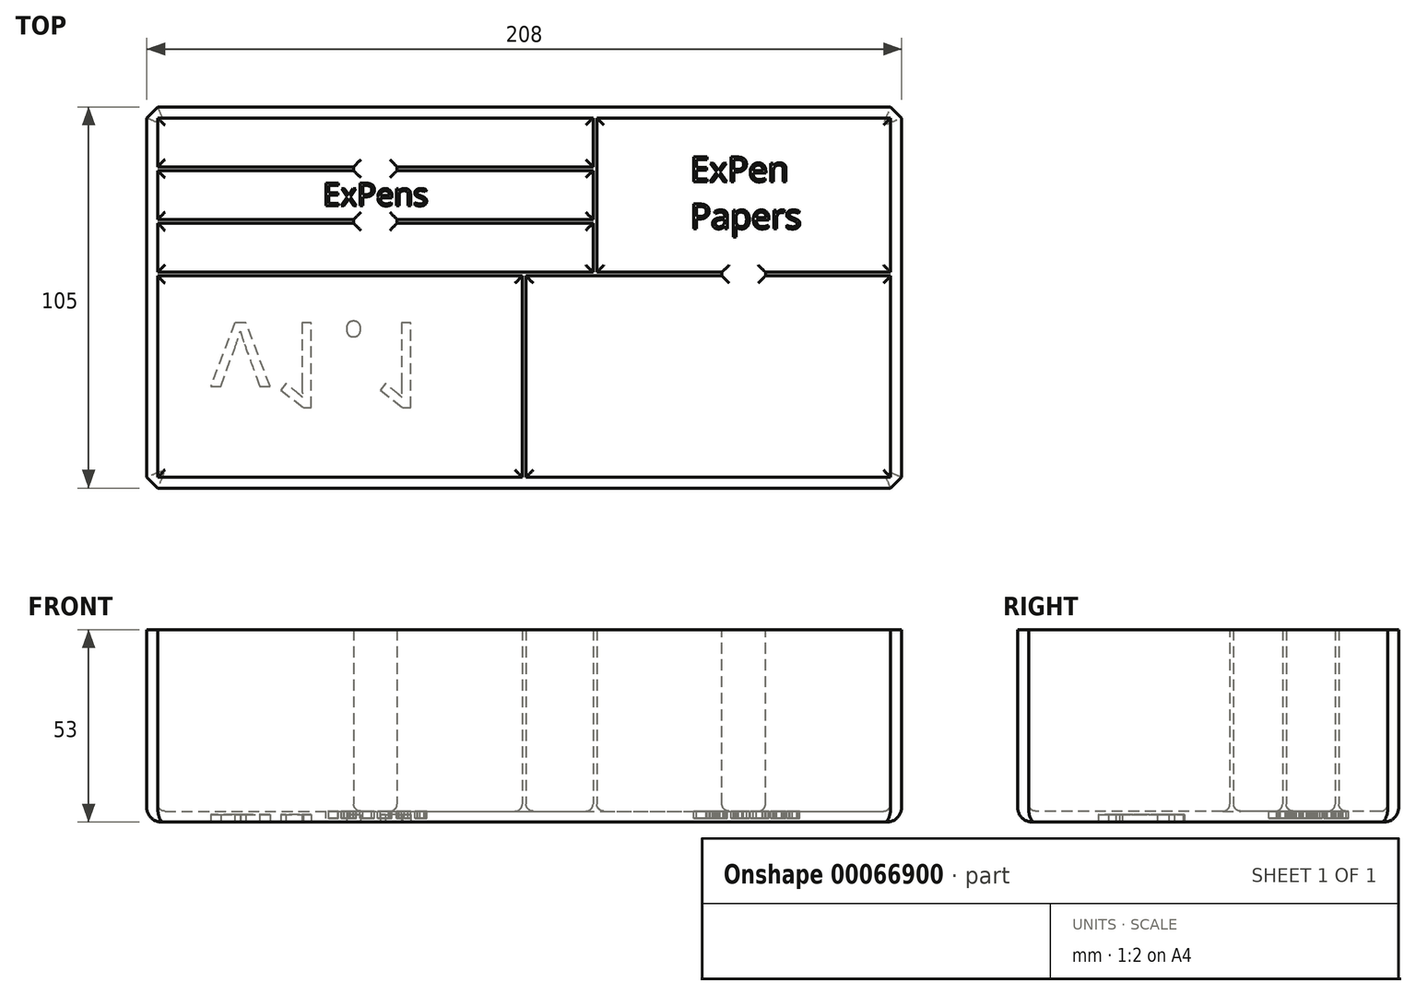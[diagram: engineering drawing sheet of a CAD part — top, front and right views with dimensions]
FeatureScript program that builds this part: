
annotation { "Feature Type Name" : "Feature", "Feature Type Description" : "" }
export const myFeature = defineFeature(function(context is Context, id is Id, definition is map)
    precondition{}
    {
        {
            var Q0;
            Q0=qCreatedBy(makeId("Top.planeOp"),FACE);
            var sketch = newSketch(context, id + "F0", { "sketchPlane" : qUnion([Q0])});
            skLineSegment(sketch, "E0.bottom", {"start": v(-42.14, 90.11) * mm, "end": v(165.86, 90.11) * mm});
            skLineSegment(sketch, "E0.top", {"start": v(-42.14, -14.89) * mm, "end": v(165.86, -14.89) * mm});
            skLineSegment(sketch, "E0.left", {"start": v(-42.14, 90.11) * mm, "end": v(-42.14, -14.89) * mm});
            skLineSegment(sketch, "E0.right", {"start": v(165.86, 90.11) * mm, "end": v(165.86, -14.89) * mm});
            skSolve(sketch);
        }
        {
            var Q0;
            Q0 = qSketchRegion(id + "F0", true);
            extrude(context, id + "F1", {"entities" : qUnion([Q0]), "depth" : 53 * mm});
        }
        {
            var Q0;
            Q0=makeQuery(id+"F1.opExtrude","CAP_FACE",FACE,{"disambiguationData":[OSD([sQuery(id+"F0.wireOp",EDGE,"E0.bottom"),sQuery(id+"F0.wireOp",EDGE,"E0.top"),sQuery(id+"F0.wireOp",EDGE,"E0.left"),sQuery(id+"F0.wireOp",EDGE,"E0.right")])],"isStart":false});
            shell(context, id + "F2", {"entities" : qUnion([Q0]), "thickness" : 3 * mm});
        }
        {
            var Q0;
            Q0=makeQuery(id+"F2.opShell","OFFSET_FACE",FACE,{"disambiguationData":[OSD([sQuery(id+"F0.wireOp",EDGE,"E0.bottom"),sQuery(id+"F0.wireOp",EDGE,"E0.top"),sQuery(id+"F0.wireOp",EDGE,"E0.left"),sQuery(id+"F0.wireOp",EDGE,"E0.right")])]});
            var sketch = newSketch(context, id + "F3", { "sketchPlane" : qUnion([Q0])});
            skLineSegment(sketch, "E1.bottom", {"start": v(-39.14, 73.61) * mm, "end": v(81.86, 73.61) * mm});
            skLineSegment(sketch, "E1.top", {"start": v(-39.14, 72.61) * mm, "end": v(81.86, 72.61) * mm});
            skLineSegment(sketch, "E1.left", {"start": v(-39.14, 73.61) * mm, "end": v(-39.14, 72.61) * mm});
            skLineSegment(sketch, "E1.right", {"start": v(162.86, 73.61) * mm, "end": v(162.86, 72.61) * mm});
            skLineSegment(sketch, "E2.bottom", {"start": v(-39.14, 59.11) * mm, "end": v(81.86, 59.11) * mm});
            skLineSegment(sketch, "E2.top", {"start": v(-39.14, 58.11) * mm, "end": v(81.86, 58.11) * mm});
            skLineSegment(sketch, "E2.left", {"start": v(-39.14, 59.11) * mm, "end": v(-39.14, 58.11) * mm});
            skLineSegment(sketch, "E2.right", {"start": v(162.86, 59.11) * mm, "end": v(162.86, 58.11) * mm});
            skLineSegment(sketch, "E3.bottom", {"start": v(-39.14, 44.61) * mm, "end": v(162.86, 44.61) * mm});
            skLineSegment(sketch, "E3.top", {"start": v(-39.14, 43.61) * mm, "end": v(162.86, 43.61) * mm});
            skLineSegment(sketch, "E3.left", {"start": v(-39.14, 44.61) * mm, "end": v(-39.14, 43.61) * mm});
            skLineSegment(sketch, "E3.right", {"start": v(162.86, 44.61) * mm, "end": v(162.86, 43.61) * mm});
            skLineSegment(sketch, "E4.bottom", {"start": v(62.36, 43.61) * mm, "end": v(61.36, 43.61) * mm});
            skLineSegment(sketch, "E4.top", {"start": v(62.36, -11.89) * mm, "end": v(61.36, -11.89) * mm});
            skLineSegment(sketch, "E4.left", {"start": v(62.36, 43.61) * mm, "end": v(62.36, -11.89) * mm});
            skLineSegment(sketch, "E4.right", {"start": v(61.36, 43.61) * mm, "end": v(61.36, -11.89) * mm});
            skLineSegment(sketch, "E5.bottom", {"start": v(80.86, 87.11) * mm, "end": v(81.86, 87.11) * mm});
            skLineSegment(sketch, "E5.top", {"start": v(80.86, 44.61) * mm, "end": v(81.86, 44.61) * mm});
            skLineSegment(sketch, "E5.left", {"start": v(80.86, 87.11) * mm, "end": v(80.86, 44.61) * mm});
            skLineSegment(sketch, "E5.right", {"start": v(81.86, 87.11) * mm, "end": v(81.86, 44.61) * mm});
            skSolve(sketch);
        }
        {
            var Q0;
            Q0 = qSketchRegion(id + "F3", true);
            extrude(context, id + "F4", {"entities" : qUnion([Q0]), "operationType" : NewBodyOperationType.ADD, "depth" : 50 * mm});
        }
        {
            var Q0;
            Q0=makeQuery(id+"F1.opExtrude","SWEPT_EDGE",EDGE,{"disambiguationData":[OSD([sQuery(id+"F0.wireOp",EDGE,"E0.top"),sQuery(id+"F0.wireOp",EDGE,"E0.right")])]});
            var Q1;
            Q1=makeQuery(id+"F1.opExtrude","SWEPT_EDGE",EDGE,{"disambiguationData":[OSD([sQuery(id+"F0.wireOp",EDGE,"E0.bottom"),sQuery(id+"F0.wireOp",EDGE,"E0.right")])]});
            var Q2;
            Q2=makeQuery(id+"F1.opExtrude","SWEPT_EDGE",EDGE,{"disambiguationData":[OSD([sQuery(id+"F0.wireOp",EDGE,"E0.top"),sQuery(id+"F0.wireOp",EDGE,"E0.left")])]});
            var Q3;
            Q3=makeQuery(id+"F1.opExtrude","SWEPT_EDGE",EDGE,{"disambiguationData":[OSD([sQuery(id+"F0.wireOp",EDGE,"E0.bottom"),sQuery(id+"F0.wireOp",EDGE,"E0.left")])]});
            chamfer(context, id + "F5", {"entities" : qUnion([Q0, Q1, Q2, Q3]), "width" : 3 * mm, "tangentPropagation" : true});
        }
        {
            var Q0;
            Q0=makeQuery(id+"F1.opExtrude","CAP_FACE",FACE,{"disambiguationData":[OSD([sQuery(id+"F0.wireOp",EDGE,"E0.bottom"),sQuery(id+"F0.wireOp",EDGE,"E0.top"),sQuery(id+"F0.wireOp",EDGE,"E0.left"),sQuery(id+"F0.wireOp",EDGE,"E0.right")])],"isStart":true});
            fillet(context, id + "F6", {"entities" : qUnion([Q0]), "radius" : 4 * mm, "tangentPropagation" : true, "allowEdgeOverflow" : false});
        }
        {
            var Q0;
            Q0=makeQuery(id+"F4.opExtrude","SWEPT_FACE",FACE,{"disambiguationData":[OSD([sQuery(id+"F3.wireOp",EDGE,"E1.top")])]});
            var sketch = newSketch(context, id + "F7", { "sketchPlane" : qUnion([Q0])});
            skPoint(sketch, "E6", {"position": v(20.86, 3) * mm});
            skLineSegment(sketch, "E7.bottom", {"start": v(26.86, 3) * mm, "end": v(14.86, 3) * mm});
            skLineSegment(sketch, "E7.top", {"start": v(26.86, 53) * mm, "end": v(14.86, 53) * mm});
            skLineSegment(sketch, "E7.left", {"start": v(26.86, 3) * mm, "end": v(26.86, 53) * mm});
            skLineSegment(sketch, "E7.right", {"start": v(14.86, 3) * mm, "end": v(14.86, 53) * mm});
            skSolve(sketch);
        }
        {
            var Q0;
            Q0=makeQuery(id+"F7.imprint","IMPRINT",FACE,{"disambiguationData":[TD([[makeQuery(id+"F7.imprint","IMPRINT",EDGE,{"derivedFrom":sQuery(id+"F7.wireOp",EDGE,"E7.bottom")}),1.0]])]});
            extrude(context, id + "F8", {"entities" : qUnion([Q0]), "operationType" : NewBodyOperationType.REMOVE, "oppositeDirection" : true, "depth" : 10 * mm, "hasSecondDirection" : true, "secondDirectionOppositeDirection" : false, "secondDirectionDepth" : 15 * mm});
        }
        {
            var Q0;
            {var subQ0=sQuery(id+"F3.wireOp",EDGE,"E3.bottom");Q0=makeQuery(id+"F4.opExtrude","SWEPT_FACE",FACE,{"disambiguationData":[OSD([subQ0]),TDD([makeQuery(id+"F3.imprint","IMPRINT",EDGE,{"disambiguationData":[TD([[makeQuery(id+"F3.imprint","INTERSECT",VERTEX,{"derivedFrom":[subQ0,sQuery(id+"F3.wireOp",EDGE,"E5.top"),sQuery(id+"F3.wireOp",EDGE,"E5.right")]}),-1.0]])],"derivedFrom":subQ0})])]});}
            var sketch = newSketch(context, id + "F9", { "sketchPlane" : qUnion([Q0])});
            skPoint(sketch, "E8", {"position": v(-122.36, 53) * mm});
            skLineSegment(sketch, "E9.bottom", {"start": v(-128.36, 3) * mm, "end": v(-116.36, 3) * mm});
            skLineSegment(sketch, "E9.top", {"start": v(-128.36, 53) * mm, "end": v(-116.36, 53) * mm});
            skLineSegment(sketch, "E9.left", {"start": v(-128.36, 3) * mm, "end": v(-128.36, 53) * mm});
            skLineSegment(sketch, "E9.right", {"start": v(-116.36, 3) * mm, "end": v(-116.36, 53) * mm});
            skSolve(sketch);
        }
        {
            var Q0;
            Q0 = qSketchRegion(id + "F9", true);
            extrude(context, id + "F10", {"entities" : qUnion([Q0]), "operationType" : NewBodyOperationType.REMOVE, "oppositeDirection" : true, "depth" : 5 * mm});
        }
        {
            var Q0;
            {var subQ0=sQuery(id+"F0.wireOp",EDGE,"E0.top");var subQ1=sQuery(id+"F0.wireOp",EDGE,"E0.left");var subQ2=sQuery(id+"F3.wireOp",EDGE,"E4.right");Q0=makeQuery(id+"F4.boolean.opBoolean","SPLIT",FACE,{"disambiguationData":[TD([makeQuery(id+"F4.opExtrude","SWEPT_FACE",FACE,{"disambiguationData":[OSD([subQ2])]})])],"derivedFrom":makeQuery(id+"F2.opShell","OFFSET_FACE",FACE,{"disambiguationData":[OSD([sQuery(id+"F0.wireOp",EDGE,"E0.bottom"),subQ0,subQ1,sQuery(id+"F0.wireOp",EDGE,"E0.right")])]})});}
            var Q1;
            {var subQ0=sQuery(id+"F0.wireOp",EDGE,"E0.top");var subQ1=sQuery(id+"F0.wireOp",EDGE,"E0.right");var subQ6=sQuery(id+"F3.wireOp",EDGE,"E4.left");var subQ7=sQuery(id+"F0.wireOp",EDGE,"E0.bottom");var subQ8=makeQuery(id+"F2.opShell","OFFSET_FACE",FACE,{"disambiguationData":[OSD([subQ7,subQ0,sQuery(id+"F0.wireOp",EDGE,"E0.left"),subQ1])]});var subQ10=sQuery(id+"F3.wireOp",EDGE,"E5.right");Q1=makeQuery(id+"F10.boolean.opBoolean","MERGE",FACE,{"derivedFrom":[makeQuery(id+"F4.boolean.opBoolean","SPLIT",FACE,{"disambiguationData":[TD([makeQuery(id+"F4.opExtrude","SWEPT_FACE",FACE,{"disambiguationData":[OSD([subQ10])]})])],"derivedFrom":subQ8}),makeQuery(id+"F4.boolean.opBoolean","SPLIT",FACE,{"disambiguationData":[TD([makeQuery(id+"F4.opExtrude","SWEPT_FACE",FACE,{"disambiguationData":[OSD([subQ6])]})])],"derivedFrom":subQ8}),makeQuery(id+"F10.opExtrude","SWEPT_FACE",FACE,{"disambiguationData":[OSD([sQuery(id+"F9.wireOp",EDGE,"E9.bottom")])]})]});}
            var Q2;
            {var subQ0=sQuery(id+"F0.wireOp",EDGE,"E0.bottom");var subQ1=sQuery(id+"F0.wireOp",EDGE,"E0.left");var subQ4=sQuery(id+"F3.wireOp",EDGE,"E1.bottom");var subQ5=makeQuery(id+"F2.opShell","OFFSET_FACE",FACE,{"disambiguationData":[OSD([subQ0,sQuery(id+"F0.wireOp",EDGE,"E0.top"),subQ1,sQuery(id+"F0.wireOp",EDGE,"E0.right")])]});var subQ8=sQuery(id+"F3.wireOp",EDGE,"E2.top");var subQ9=sQuery(id+"F3.wireOp",EDGE,"E1.top");Q2=makeQuery(id+"F8.boolean.opBoolean","MERGE",FACE,{"derivedFrom":[makeQuery(id+"F4.boolean.opBoolean","SPLIT",FACE,{"disambiguationData":[TD([makeQuery(id+"F4.opExtrude","SWEPT_FACE",FACE,{"disambiguationData":[OSD([subQ9])]})])],"derivedFrom":subQ5}),makeQuery(id+"F4.boolean.opBoolean","SPLIT",FACE,{"disambiguationData":[TD([makeQuery(id+"F4.opExtrude","SWEPT_FACE",FACE,{"disambiguationData":[OSD([subQ8])]})])],"derivedFrom":subQ5}),makeQuery(id+"F4.boolean.opBoolean","SPLIT",FACE,{"disambiguationData":[TD([makeQuery(id+"F4.opExtrude","SWEPT_FACE",FACE,{"disambiguationData":[OSD([subQ4])]})])],"derivedFrom":subQ5}),makeQuery(id+"F8.opExtrude","SWEPT_FACE",FACE,{"disambiguationData":[OSD([sQuery(id+"F7.wireOp",EDGE,"E7.bottom")])]})]});}
            fillet(context, id + "F11", {"entities" : qUnion([Q0, Q1, Q2]), "radius" : 2 * mm, "tangentPropagation" : true, "allowEdgeOverflow" : false});
        }
        {
            var Q0;
            Q0=makeQuery(id+"F1.opExtrude","CAP_FACE",FACE,{"disambiguationData":[OSD([sQuery(id+"F0.wireOp",EDGE,"E0.bottom"),sQuery(id+"F0.wireOp",EDGE,"E0.top"),sQuery(id+"F0.wireOp",EDGE,"E0.left"),sQuery(id+"F0.wireOp",EDGE,"E0.right")])],"isStart":true});
            var sketch = newSketch(context, id + "F12", { "sketchPlane" : qUnion([Q0])});
            skText(sketch, "E10", { "text": "v1.1", "fontName": "OpenSans-Regular.ttf"});
            const initialGuessF12  = {"E10": [-0.02454, -0.03067, 1, 0, 0.02353]};
            skSetInitialGuess(sketch, initialGuessF12);
            skSolve(sketch);
        }
        {
            var Q0;
            Q0 = qSketchRegion(id + "F12", true);
            extrude(context, id + "F13", {"entities" : qUnion([Q0]), "operationType" : NewBodyOperationType.REMOVE, "oppositeDirection" : true, "depth" : 2 * mm});
        }
        {
            var Q0;
            {var subQ0=sQuery(id+"F0.wireOp",EDGE,"E0.top");var subQ1=sQuery(id+"F0.wireOp",EDGE,"E0.right");var subQ6=sQuery(id+"F3.wireOp",EDGE,"E4.left");var subQ7=sQuery(id+"F0.wireOp",EDGE,"E0.bottom");var subQ8=makeQuery(id+"F2.opShell","OFFSET_FACE",FACE,{"disambiguationData":[OSD([subQ7,subQ0,sQuery(id+"F0.wireOp",EDGE,"E0.left"),subQ1])]});var subQ10=sQuery(id+"F3.wireOp",EDGE,"E5.right");Q0=makeQuery(id+"F10.boolean.opBoolean","MERGE",FACE,{"derivedFrom":[makeQuery(id+"F4.boolean.opBoolean","SPLIT",FACE,{"disambiguationData":[TD([makeQuery(id+"F4.opExtrude","SWEPT_FACE",FACE,{"disambiguationData":[OSD([subQ10])]})])],"derivedFrom":subQ8}),makeQuery(id+"F4.boolean.opBoolean","SPLIT",FACE,{"disambiguationData":[TD([makeQuery(id+"F4.opExtrude","SWEPT_FACE",FACE,{"disambiguationData":[OSD([subQ6])]})])],"derivedFrom":subQ8}),makeQuery(id+"F10.opExtrude","SWEPT_FACE",FACE,{"disambiguationData":[OSD([sQuery(id+"F9.wireOp",EDGE,"E9.bottom")])]})]});}
            var sketch = newSketch(context, id + "F14", { "sketchPlane" : qUnion([Q0])});
            skText(sketch, "E11", { "text": "ExPen\nPapers", "fontName": "OpenSans-Regular.ttf"});
            const initialGuessF14  = {"E11": [0.1076, 0.06955, 1, 0, 0.00686]};
            skSetInitialGuess(sketch, initialGuessF14);
            skSolve(sketch);
        }
        {
            var Q0;
            Q0 = qSketchRegion(id + "F14", true);
            extrude(context, id + "F15", {"entities" : qUnion([Q0]), "operationType" : NewBodyOperationType.REMOVE, "oppositeDirection" : true, "depth" : 2 * mm});
        }
        {
            var Q0;
            {var subQ0=sQuery(id+"F0.wireOp",EDGE,"E0.bottom");var subQ1=sQuery(id+"F0.wireOp",EDGE,"E0.left");var subQ4=sQuery(id+"F3.wireOp",EDGE,"E1.bottom");var subQ5=makeQuery(id+"F2.opShell","OFFSET_FACE",FACE,{"disambiguationData":[OSD([subQ0,sQuery(id+"F0.wireOp",EDGE,"E0.top"),subQ1,sQuery(id+"F0.wireOp",EDGE,"E0.right")])]});var subQ8=sQuery(id+"F3.wireOp",EDGE,"E2.top");var subQ9=sQuery(id+"F3.wireOp",EDGE,"E1.top");Q0=makeQuery(id+"F8.boolean.opBoolean","MERGE",FACE,{"derivedFrom":[makeQuery(id+"F4.boolean.opBoolean","SPLIT",FACE,{"disambiguationData":[TD([makeQuery(id+"F4.opExtrude","SWEPT_FACE",FACE,{"disambiguationData":[OSD([subQ9])]})])],"derivedFrom":subQ5}),makeQuery(id+"F4.boolean.opBoolean","SPLIT",FACE,{"disambiguationData":[TD([makeQuery(id+"F4.opExtrude","SWEPT_FACE",FACE,{"disambiguationData":[OSD([subQ8])]})])],"derivedFrom":subQ5}),makeQuery(id+"F4.boolean.opBoolean","SPLIT",FACE,{"disambiguationData":[TD([makeQuery(id+"F4.opExtrude","SWEPT_FACE",FACE,{"disambiguationData":[OSD([subQ4])]})])],"derivedFrom":subQ5}),makeQuery(id+"F8.opExtrude","SWEPT_FACE",FACE,{"disambiguationData":[OSD([sQuery(id+"F7.wireOp",EDGE,"E7.bottom")])]})]});}
            var sketch = newSketch(context, id + "F16", { "sketchPlane" : qUnion([Q0])});
            skText(sketch, "E12", { "text": "ExPens", "fontName": "OpenSans-Regular.ttf"});
            const initialGuessF16  = {"E12": [0.00642, 0.06292, 1, 0, 0.00626]};
            skSetInitialGuess(sketch, initialGuessF16);
            skSolve(sketch);
        }
        {
            var Q0;
            Q0 = qSketchRegion(id + "F16", true);
            extrude(context, id + "F17", {"entities" : qUnion([Q0]), "operationType" : NewBodyOperationType.REMOVE, "oppositeDirection" : true, "depth" : 2 * mm});
        }
    });
